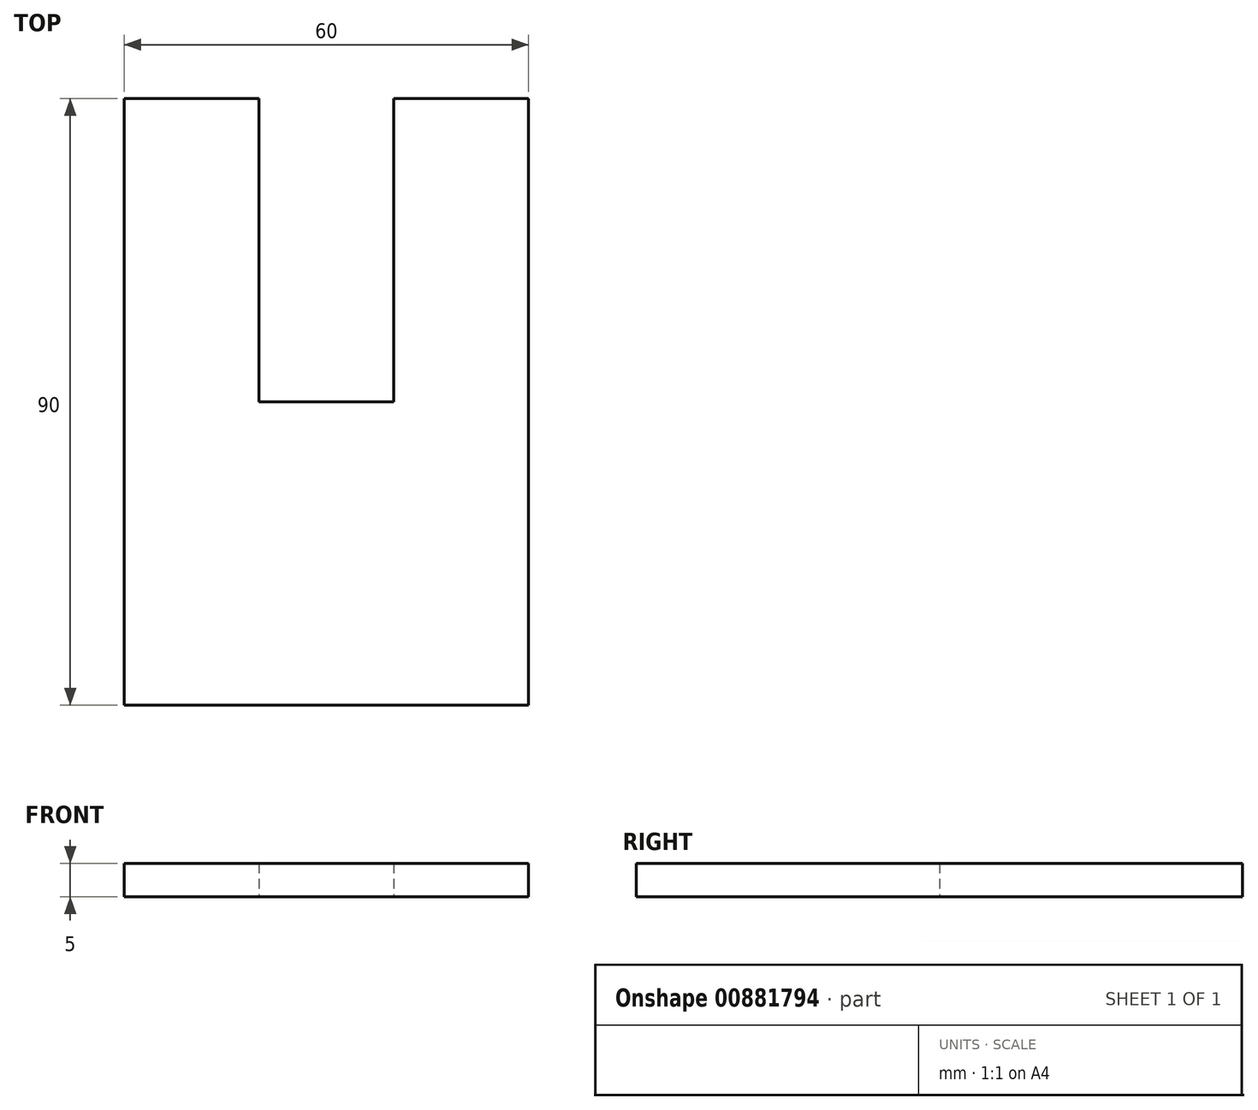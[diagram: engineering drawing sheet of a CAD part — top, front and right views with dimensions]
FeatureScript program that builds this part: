
annotation { "Feature Type Name" : "Feature", "Feature Type Description" : "" }
export const myFeature = defineFeature(function(context is Context, id is Id, definition is map)
    precondition{}
    {
        {
            var Q0;
            Q0=qCreatedBy(makeId("Top.planeOp"),FACE);
            var sketch = newSketch(context, id + "F0", { "sketchPlane" : qUnion([Q0])});
            skLineSegment(sketch, "E0", {"start": v(0, 0) * mm, "end": v(0, 90) * mm, "construction": true});
            skLineSegment(sketch, "E1", {"start": v(0, 90) * mm, "end": v(-10, 90) * mm, "construction": true});
            skLineSegment(sketch, "E2", {"start": v(-10, 90) * mm, "end": v(-30, 90) * mm});
            skLineSegment(sketch, "E3", {"start": v(-30, 90) * mm, "end": v(-30, 0) * mm});
            skLineSegment(sketch, "E4", {"start": v(-30, 0) * mm, "end": v(0, 0) * mm});
            skLineSegment(sketch, "E5", {"start": v(-10, 90) * mm, "end": v(-10, 45) * mm});
            skLineSegment(sketch, "E6", {"start": v(-10, 45) * mm, "end": v(0, 45) * mm});
            skLineSegment(sketch, "E7.MirrorCS", {"start": v(10, 45) * mm, "end": v(0, 45) * mm});
            skLineSegment(sketch, "E8.MirrorCS", {"start": v(10, 90) * mm, "end": v(10, 45) * mm});
            skLineSegment(sketch, "E9.MirrorCS", {"start": v(10, 90) * mm, "end": v(30, 90) * mm});
            skLineSegment(sketch, "E10.MirrorCS", {"start": v(30, 90) * mm, "end": v(30, 0) * mm});
            skLineSegment(sketch, "E11.MirrorCS", {"start": v(30, 0) * mm, "end": v(0, 0) * mm});
            skSolve(sketch);
        }
        {
            var Q0;
            Q0=qSketchRegion(id+"F0",true);
            extrude(context, id + "F1", {"entities" : qUnion([Q0]), "depth" : 5 * mm, "offsetDistance" : 25 * mm});
        }
    });
